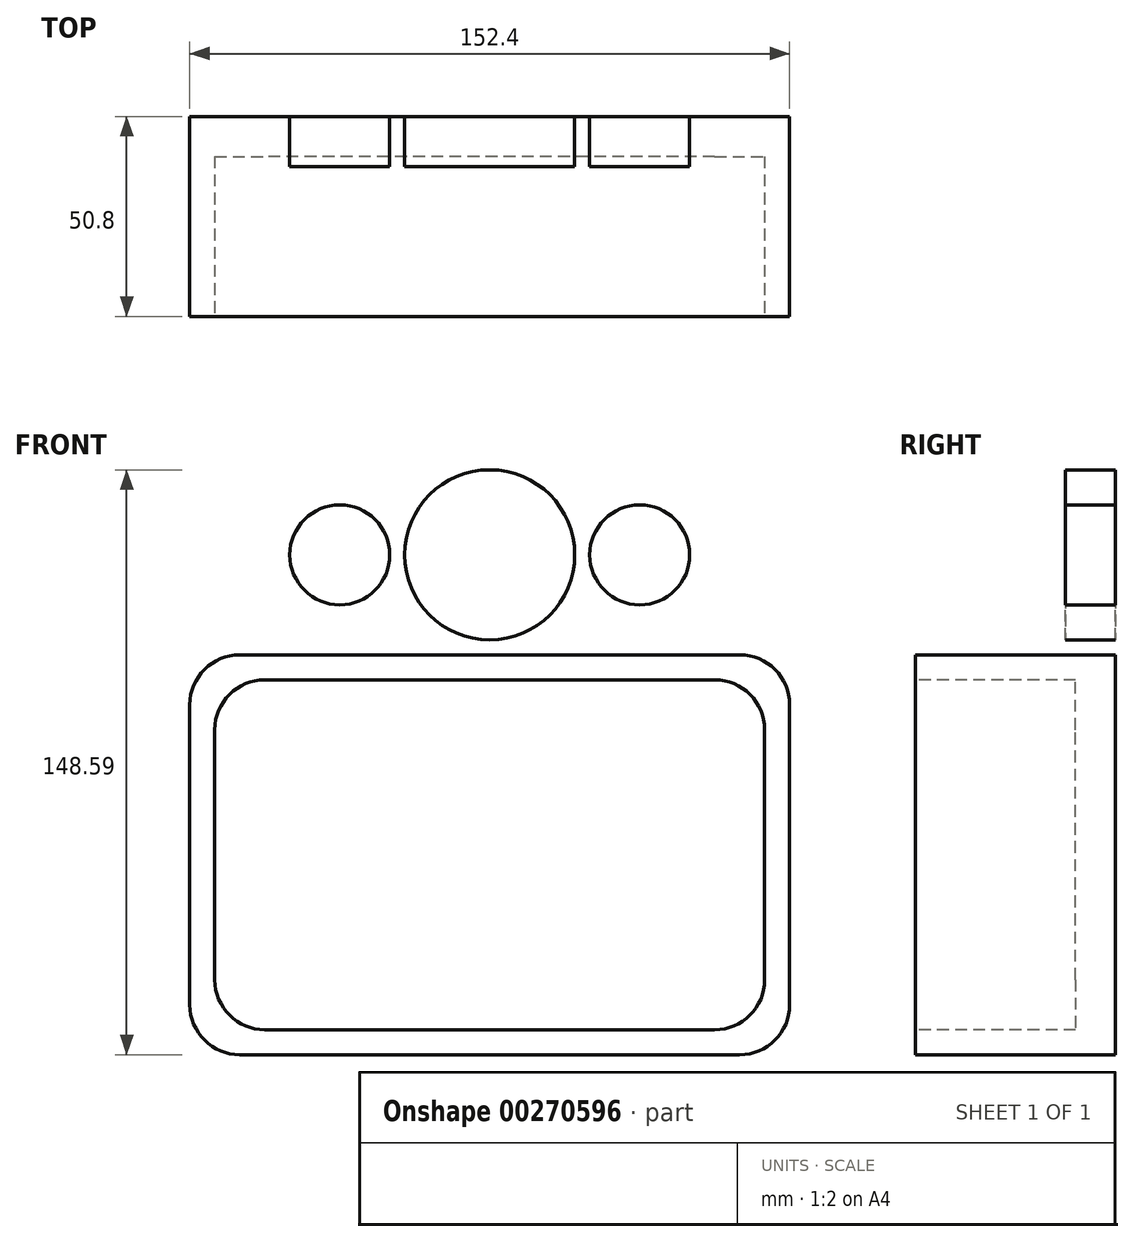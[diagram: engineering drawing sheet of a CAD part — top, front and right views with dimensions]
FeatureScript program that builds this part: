
annotation { "Feature Type Name" : "Feature", "Feature Type Description" : "" }
export const myFeature = defineFeature(function(context is Context, id is Id, definition is map)
    precondition{}
    {
        {
            var Q0;
            Q0=qCreatedBy(makeId("Front.planeOp"),FACE);
            var sketch = newSketch(context, id + "F0", { "sketchPlane" : qUnion([Q0])});
            skLineSegment(sketch, "E0.bottom", {"start": v(63.5, -50.8) * mm, "end": v(-63.5, -50.8) * mm});
            skLineSegment(sketch, "E0.top", {"start": v(63.5, 50.8) * mm, "end": v(-63.5, 50.8) * mm});
            skLineSegment(sketch, "E0.left", {"start": v(76.2, -38.1) * mm, "end": v(76.2, 38.1) * mm});
            skLineSegment(sketch, "E0.right", {"start": v(-76.2, -38.1) * mm, "end": v(-76.2, 38.1) * mm});
            skPoint(sketch, "E0.middle", {"position": v(0, 0) * mm});
            skPoint(sketch, "E1.visualSharp", {"position": v(-76.2, 50.8) * mm});
            skArc(sketch, "E1.filletArc", {"start": v(-63.5, 50.8) * mm, "mid": v(-72.48, 47.08) * mm, "end": v(-76.2, 38.1) * mm});
            skPoint(sketch, "E2.visualSharp", {"position": v(76.2, 50.8) * mm});
            skArc(sketch, "E2.filletArc", {"start": v(76.2, 38.1) * mm, "mid": v(72.48, 47.08) * mm, "end": v(63.5, 50.8) * mm});
            skPoint(sketch, "E3.visualSharp", {"position": v(76.2, -50.8) * mm});
            skArc(sketch, "E3.filletArc", {"start": v(63.5, -50.8) * mm, "mid": v(72.48, -47.08) * mm, "end": v(76.2, -38.1) * mm});
            skPoint(sketch, "E4.visualSharp", {"position": v(-76.2, -50.8) * mm});
            skArc(sketch, "E4.filletArc", {"start": v(-76.2, -38.1) * mm, "mid": v(-72.48, -47.08) * mm, "end": v(-63.5, -50.8) * mm});
            skLineSegment(sketch, "E5.bottom", {"start": v(-63.5, 50.8) * mm, "end": v(63.5, 50.8) * mm});
            skLineSegment(sketch, "E5.top", {"start": v(-63.5, 101.6) * mm, "end": v(63.5, 101.6) * mm});
            skLineSegment(sketch, "E5.left", {"start": v(-63.5, 50.8) * mm, "end": v(-63.5, 101.6) * mm});
            skLineSegment(sketch, "E5.right", {"start": v(63.5, 50.8) * mm, "end": v(63.5, 101.6) * mm});
            skLineSegment(sketch, "E6", {"start": v(-63.5, 101.6) * mm, "end": v(-38.1, 101.6) * mm});
            skLineSegment(sketch, "E7", {"start": v(-38.1, 101.6) * mm, "end": v(-38.1, 76.2) * mm});
            skCircle(sketch, "E8", {"center": v(-38.1, 76.2) * mm, "radius": 12.7 * mm});
            skLineSegment(sketch, "E9", {"start": v(63.5, 101.6) * mm, "end": v(63.5, 76.2) * mm});
            skLineSegment(sketch, "E10", {"start": v(63.5, 76.2) * mm, "end": v(38.1, 76.2) * mm});
            skCircle(sketch, "E11", {"center": v(38.1, 76.2) * mm, "radius": 12.7 * mm});
            skLineSegment(sketch, "E12", {"start": v(-63.5, 101.6) * mm, "end": v(0, 101.6) * mm});
            skLineSegment(sketch, "E13", {"start": v(0, 101.6) * mm, "end": v(0, 76.2) * mm});
            skCircle(sketch, "E14", {"center": v(0, 76.2) * mm, "radius": 21.59 * mm});
            skSolve(sketch);
        }
        {
            var Q0;
            Q0=makeQuery(id+"F0.imprint","IMPRINT",FACE,{"disambiguationData":[TD([[makeQuery(id+"F0.imprint","IMPRINT",EDGE,{"derivedFrom":sQuery(id+"F0.wireOp",EDGE,"E0.bottom")}),-1.0]])]});
            extrude(context, id + "F1", {"entities" : qUnion([Q0]), "oppositeDirection" : true, "depth" : 50.8 * mm});
        }
        {
            var Q0;
            Q0=makeQuery(id+"F1.opExtrude","CAP_FACE",FACE,{"disambiguationData":[OSD([sQuery(id+"F0.wireOp",EDGE,"E0.bottom"),sQuery(id+"F0.wireOp",EDGE,"E0.top"),sQuery(id+"F0.wireOp",EDGE,"E0.left"),sQuery(id+"F0.wireOp",EDGE,"E0.right"),sQuery(id+"F0.wireOp",EDGE,"E1.filletArc"),sQuery(id+"F0.wireOp",EDGE,"E2.filletArc"),sQuery(id+"F0.wireOp",EDGE,"E3.filletArc"),sQuery(id+"F0.wireOp",EDGE,"E4.filletArc")])],"isStart":true});
            var sketch = newSketch(context, id + "F2", { "sketchPlane" : qUnion([Q0])});
            skLineSegment(sketch, "E15.bottom", {"start": v(57.15, -44.45) * mm, "end": v(-57.15, -44.45) * mm});
            skLineSegment(sketch, "E15.top", {"start": v(57.15, 44.45) * mm, "end": v(-57.15, 44.45) * mm});
            skLineSegment(sketch, "E15.left", {"start": v(69.85, -31.75) * mm, "end": v(69.85, 31.75) * mm});
            skLineSegment(sketch, "E15.right", {"start": v(-69.85, -31.75) * mm, "end": v(-69.85, 31.75) * mm});
            skPoint(sketch, "E15.middle", {"position": v(0, 0) * mm});
            skPoint(sketch, "E16.visualSharp", {"position": v(-69.85, 44.45) * mm});
            skArc(sketch, "E16.filletArc", {"start": v(-57.15, 44.45) * mm, "mid": v(-66.13, 40.73) * mm, "end": v(-69.85, 31.75) * mm});
            skPoint(sketch, "E17.visualSharp", {"position": v(-69.85, -44.45) * mm});
            skArc(sketch, "E17.filletArc", {"start": v(-69.85, -31.75) * mm, "mid": v(-66.13, -40.73) * mm, "end": v(-57.15, -44.45) * mm});
            skPoint(sketch, "E18.visualSharp", {"position": v(69.85, -44.45) * mm});
            skArc(sketch, "E18.filletArc", {"start": v(57.15, -44.45) * mm, "mid": v(66.13, -40.73) * mm, "end": v(69.85, -31.75) * mm});
            skPoint(sketch, "E19.visualSharp", {"position": v(69.85, 44.45) * mm});
            skArc(sketch, "E19.filletArc", {"start": v(69.85, 31.75) * mm, "mid": v(66.13, 40.73) * mm, "end": v(57.15, 44.45) * mm});
            skSolve(sketch);
        }
        {
            var Q0;
            Q0=makeQuery(id+"F2.imprint","IMPRINT",FACE,{"disambiguationData":[TD([[makeQuery(id+"F2.imprint","IMPRINT",EDGE,{"derivedFrom":sQuery(id+"F2.wireOp",EDGE,"E15.bottom")}),-1.0]])]});
            extrude(context, id + "F3", {"entities" : qUnion([Q0]), "operationType" : NewBodyOperationType.REMOVE, "oppositeDirection" : true, "depth" : 40.64 * mm});
        }
        {
            var Q0;
            Q0=makeQuery(id+"F0.imprint","IMPRINT",FACE,{"disambiguationData":[TD([[makeQuery(id+"F0.imprint","IMPRINT",EDGE,{"derivedFrom":sQuery(id+"F0.wireOp",EDGE,"E5.bottom")}),1.0]])]});
            var Q1;
            Q1=makeQuery(id+"F0.imprint","IMPRINT",FACE,{"disambiguationData":[TD([[makeQuery(id+"F0.imprint","IMPRINT",EDGE,{"derivedFrom":sQuery(id+"F0.wireOp",EDGE,"E11")}),1.0]])]});
            var Q2;
            Q2=makeQuery(id+"F0.imprint","IMPRINT",FACE,{"disambiguationData":[TD([[makeQuery(id+"F0.imprint","IMPRINT",EDGE,{"derivedFrom":sQuery(id+"F0.wireOp",EDGE,"E14")}),1.0]])]});
            var Q3;
            Q3=makeQuery(id+"F0.imprint","IMPRINT",FACE,{"disambiguationData":[TD([[makeQuery(id+"F0.imprint","IMPRINT",EDGE,{"derivedFrom":sQuery(id+"F0.wireOp",EDGE,"E8")}),1.0]])]});
            extrude(context, id + "F4", {"entities" : qUnion([Q0, Q1, Q2, Q3]), "operationType" : NewBodyOperationType.ADD, "oppositeDirection" : true, "depth" : 50.8 * mm});
        }
        {
            var Q0;
            Q0=makeQuery(id+"F0.imprint","IMPRINT",FACE,{"disambiguationData":[TD([[makeQuery(id+"F0.imprint","IMPRINT",EDGE,{"derivedFrom":sQuery(id+"F0.wireOp",EDGE,"E8")}),1.0]])]});
            var Q1;
            Q1=makeQuery(id+"F0.imprint","IMPRINT",FACE,{"disambiguationData":[TD([[makeQuery(id+"F0.imprint","IMPRINT",EDGE,{"derivedFrom":sQuery(id+"F0.wireOp",EDGE,"E14")}),1.0]])]});
            var Q2;
            Q2=makeQuery(id+"F0.imprint","IMPRINT",FACE,{"disambiguationData":[TD([[makeQuery(id+"F0.imprint","IMPRINT",EDGE,{"derivedFrom":sQuery(id+"F0.wireOp",EDGE,"E11")}),1.0]])]});
            extrude(context, id + "F5", {"entities" : qUnion([Q0, Q1, Q2]), "operationType" : NewBodyOperationType.REMOVE, "oppositeDirection" : true, "depth" : 38.1 * mm});
        }
    });
